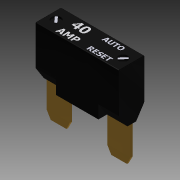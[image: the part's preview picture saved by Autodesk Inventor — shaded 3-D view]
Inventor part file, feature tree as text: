
AUTODESK INVENTOR PART (.ipt)
format: ipt  version: 2013 (Build 170138000, 138)  size: 479,232 bytes
history: native  units: in
note: dims shown in document units (in); Inventor stores cm internally (conversion verified against a paired STEP export)
features: sketch x7, chamfer x6, extrude x5, plane x5, mirror x4, emboss x2, split x1, fillet x1
ambient origin geometry x8: Origin, YZ Plane, XZ Plane, XY Plane, X Axis, Y Axis, Z Axis, Center Point
bodies: Solid1 (feature_tree)
feature tree (31):
  extrude  "Extrusion1"  Depth=0.72in
  extrude  "Extrusion2"  Depth=0.18in
  plane  "Work Plane1"
  mirror  "Mirror1"
  plane  "Work Plane2"
  mirror  "Mirror2"
  extrude  "Extrusion4"  Depth=0.28in TaperAngle=0.0deg
  chamfer  "Chamfer1"  Distance=0.49in
  chamfer  "Chamfer2"  Distance=0.1in Angle=45.0deg
  chamfer  "Chamfer3"  Distance=0.1in Angle=45.0deg
  chamfer  "Chamfer4"  Distance=0.1in Angle=45.0deg
  plane  "Work Plane3"
  mirror  "Mirror3"
  chamfer  "Chamfer5"  Distance=0.1in Angle=45.0deg
  chamfer  "Chamfer6"  Distance=0.05in Angle=45.0deg
  split  "Split1"
  extrude  "Extrusion5"  Depth=0.125in
  plane  "Work Plane4"
  emboss  "Emboss1"
  fillet  "Fillet1"  Radius=0.025in
  plane  "Work Plane5"
  emboss  "Emboss4"
  extrude  "Extrusion7"  Depth=0.1875in
  mirror  "Mirror4"
  sketch  "Sketch1"  dims[d0=1.14in d1=0.72in]
  sketch  "Sketch2"  dims[d2=0.35in d3=0.0in d4=0.18in]
  sketch  "Sketch4"  dims[d5=0.1167in d6=0.28in d7=0.0in]
  sketch  "Sketch5"  dims[d13=0.315in]
  sketch  "Sketch6"  dims[d14=0.032in d15=0.49in d16=0.0in d17=0.1in d18=0.05in d19=45.0deg d20=0.1in d21=0.05in d22=45.0deg d23=0.1in d24=0.005in d25=45.0deg d26=0.1in d27=0.005in d28=45.0deg]
  sketch  "Sketch9"  dims[d29=0.0in d30=0.05in d31=0.1in d32=45.0deg]
  sketch  "Sketch10"  dims[d33=0.05in d34=0.1in d35=45.0deg d36=0.125in d37=0.025in d38=0.0in d39=0.1875in d41=0.001in d42=0.0in d43=0.01in d50=0.125in d51=0.0001in d52=0.0in d53=0.03in d56=1.0in d57=0.0in d58=0.456in d59=0.456in]
